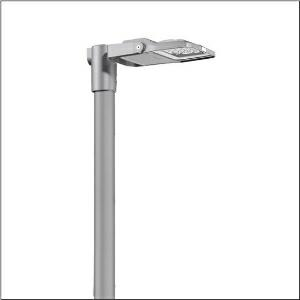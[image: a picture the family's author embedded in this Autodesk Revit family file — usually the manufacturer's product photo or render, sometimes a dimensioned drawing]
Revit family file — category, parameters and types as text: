
# Revit family: floodlight_fl_21_micro___pl61_5xa7762a2c3a_abb2
name_source: partatom
category: Lighting Fixtures
units: mm (PartAtom-declared; Revit-internal decimal feet)

## family parameters
Cut with Voids When Loaded = No
Host = Face
Light Source = No
Part Type = Normal
Room Calculation Point = No
Round Connector Dimension = Use Diameter
Shared = No

## types (1)
- --- (1 x LED, 2910 lm, 23.1 W, 3000K)
    Apparent Load = 23 VA
    CIE Flux Codes = 33 65 98 100 100
    Color Rendering = 70
    Color Temperature = 3000K
    Default Elevation = 1800 mm
    Description = Floodlight FL 21 micro, floodlight, primary light control with lens, of PMMA, primary optical cover: protective disc, of toughened safety glass, transparent, light distribution: PL61, light emission: direct distribution, installation type: surface-mounted, LED, High Power LED, rated luminous flux: 2.910lm, luminous efficacy: 126lm/W, light colour: 730, colour temperature: 3000K, control gear: ECG iQ, control: Auto-Match, Temp-Guard, Night-Set, Smart-Wire, Desk-Remote (wireless, voltage-free reading and setting of iQ features in the workshop via application-optimized NFC function/RFID function), optimised constant luminous flux control (CLO 2.0), Street-Remote, with terminal, 6-pole, mains connection: 220..240V, AC, 50/60Hz, start of lifetime: 23W, end of lifetime: 24W, reduction: 11W, luminaire housing, of diecast aluminium, powder-coated, Siteco® metallic grey (DB 702S), corrosivity category C5 according to DIN EN ISO 12944, mast bracket, of steel, galvanised, powder-coated, Siteco® metallic grey (DB 702S), protection rating (complete): IP66, insulation class (complete): insulation class II (safety insulation), certification: CE, protection symbol: D, impact resistance: IK07, permissible operating ambient temperature: -40..+40°C, permissible operating ambient temperature for outdoor applications: -40..+50°C, standard: DIN EN 12944, packaging unit: 1 piece

Light Distribution: PL61
    Height = 65 mm
    Lamp = 1 x LED
    Lamp Light Flux = 2910 lm
    Lamp Power = 23.1 W
    Lamp count = 1
    Length = 312 mm
    Luminous efficacy = 126 lm/W
    Manufacturer = Siteco
    ModVariant = No
    Model = 5XA7762A2C3A
    Number of Poles = 1
    OnlyDefault = Yes
    Power Factor = 1
    Product Name = Floodlight FL 21 micro | PL61
    Product group = floodlight | pylon top
    ProductGroupID = 6101
    Protection Class = Protection class II
    Protection Degree = IP 66
    RLX_Detail_Level = 1
    RlxData = <blob elided: 101721 chars, md5=a91c078e>
    Socket = socket
    Standby Power = 0 W
    System Light Flux = 2910 lm
    System Power = 23 W
    Type Comments = factory setting: luminous flux: 100 % | dim-lin: 254 | 455 mA
    Type Image = l_1007121.jpg
    URL = http://relux.com
    VarID = @adj_115291
    Voltage = 0 V
    Weight = 0.00 kg
    Width = 230 mm

## geometry (parser evidence)
native form markers: Blend x4, Sweep x13
no freeform markers — native parametric forms only
